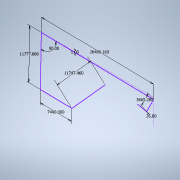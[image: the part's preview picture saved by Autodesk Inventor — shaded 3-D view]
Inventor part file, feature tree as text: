
AUTODESK INVENTOR PART (.ipt)
format: ipt  version: 2021 (Build 250183000, 183)  size: 96,256 bytes
history: native  units: in
note: dims shown in document units (in); Inventor stores cm internally (conversion verified against a paired STEP export)
features: sketch x1
ambient origin geometry x8: Origin, YZ Plane, XZ Plane, XY Plane, X Axis, Y Axis, Z Axis, Center Point
feature tree (1):
  sketch  "Sketch1"  dims[d0=26486.16in d1=0.0069in d2=3665.28in d3=0.1787in d4=11777.88in d5=90.0deg d6=7440.0in d7=11747.46in]
